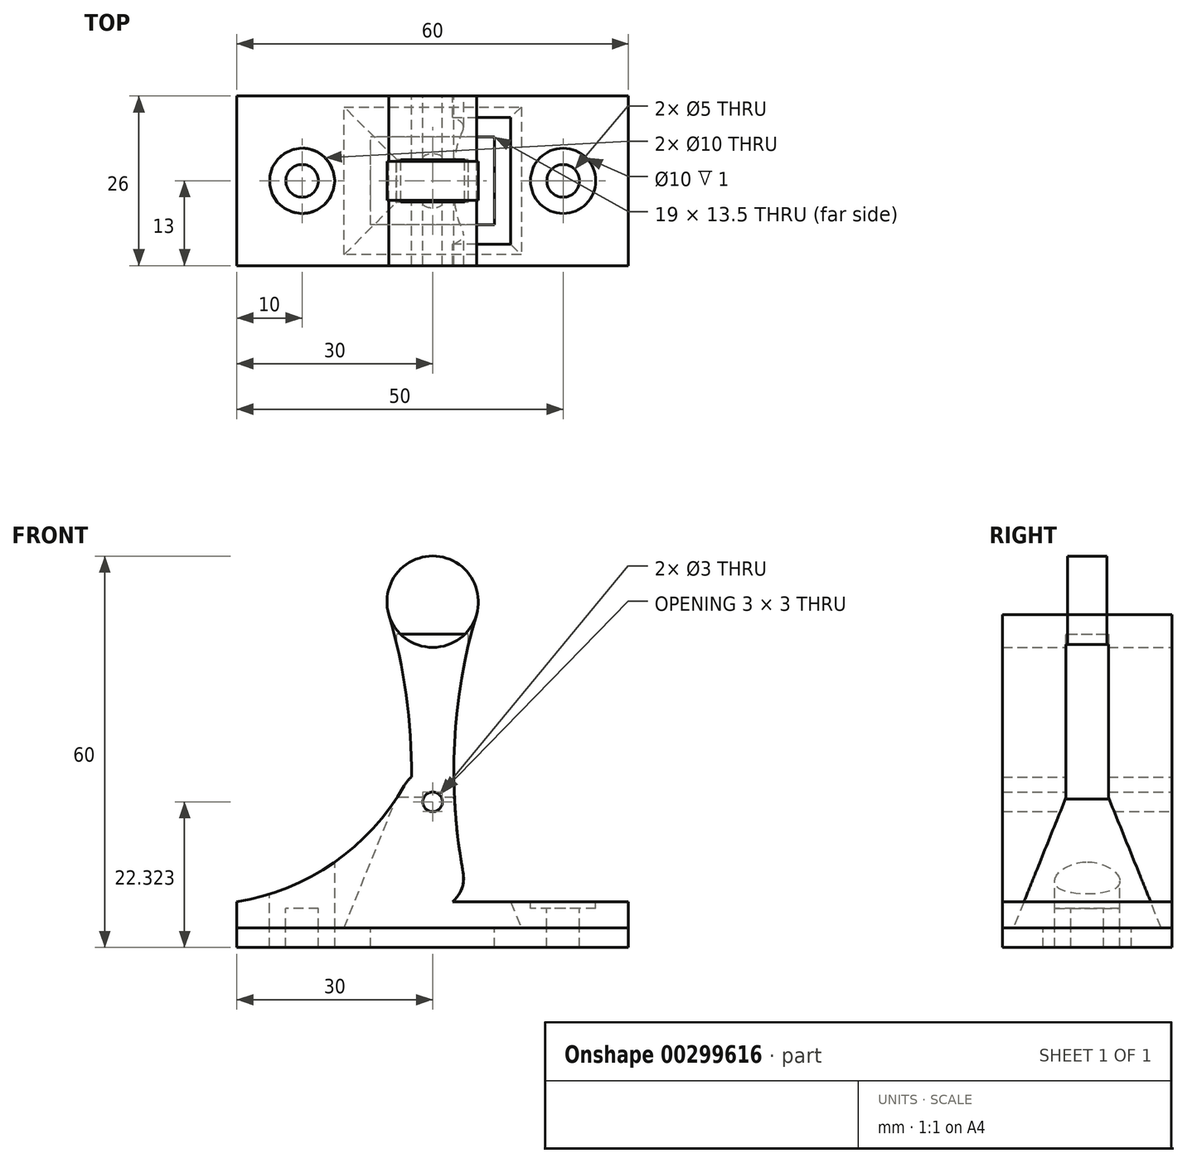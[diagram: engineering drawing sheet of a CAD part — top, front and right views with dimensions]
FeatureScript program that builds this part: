
annotation { "Feature Type Name" : "Feature", "Feature Type Description" : "" }
export const myFeature = defineFeature(function(context is Context, id is Id, definition is map)
    precondition{}
    {
        {
            var Q0;
            Q0=qCreatedBy(makeId("Front.planeOp"),FACE);
            var sketch = newSketch(context, id + "F0", { "sketchPlane" : qUnion([Q0])});
            skCircle(sketch, "E0", {"center": v(0, -12.35) * mm, "radius": 4.75 * mm});
            skCircle(sketch, "E1", {"center": v(0, 30) * mm, "radius": 7 * mm});
            skArc(sketch, "E2", {"start": v(-4.67, -11.48) * mm, "mid": v(-3.36, 8.39) * mm, "end": v(-6.71, 28.02) * mm});
            skArc(sketch, "E3.MirrorCS", {"start": v(4.67, -11.48) * mm, "mid": v(3.36, 8.39) * mm, "end": v(6.71, 28.02) * mm});
            skCircle(sketch, "E4", {"center": v(0, -0.68) * mm, "radius": 1.5 * mm});
            skCircle(sketch, "E5", {"center": v(0, -0.68) * mm, "radius": 5 * mm});
            skLineSegment(sketch, "E6.bottom", {"start": v(30, -20) * mm, "end": v(-30, -20) * mm});
            skLineSegment(sketch, "E6.top", {"start": v(30, -16) * mm, "end": v(-30, -16) * mm});
            skLineSegment(sketch, "E6.left", {"start": v(30, -20) * mm, "end": v(30, -16) * mm});
            skLineSegment(sketch, "E6.right", {"start": v(-30, -20) * mm, "end": v(-30, -16) * mm});
            skPoint(sketch, "E6.middle", {"position": v(0, -18) * mm});
            skArc(sketch, "E7", {"start": v(-30, -16) * mm, "mid": v(-15.16, -10) * mm, "end": v(-4.34, 1.8) * mm});
            skArc(sketch, "E8.MirrorCS", {"start": v(30, -16) * mm, "mid": v(15.16, -10) * mm, "end": v(4.34, 1.8) * mm});
            skSolve(sketch);
        }
        {
            var Q0;
            {var subQ0=sQuery(id+"F0.wireOp",EDGE,"E1");var subQ1=makeQuery(id+"F0.imprint","INTERSECT",VERTEX,{"derivedFrom":[subQ0,sQuery(id+"F0.wireOp",EDGE,"E2")]});Q0=makeQuery(id+"F0.imprint","IMPRINT",FACE,{"disambiguationData":[TD([[makeQuery(id+"F0.imprint","IMPRINT",EDGE,{"disambiguationData":[TD([[subQ1,-1.0]])],"derivedFrom":subQ0}),1.0]])]});}
            var Q1;
            {var subQ0=sQuery(id+"F0.wireOp",EDGE,"E3.MirrorCS");var subQ1=sQuery(id+"F0.wireOp",EDGE,"E0");var subQ2=makeQuery(id+"F0.imprint","INTERSECT",VERTEX,{"disambiguationData":[OD(1.0)],"derivedFrom":[subQ1,subQ0]});Q1=makeQuery(id+"F0.imprint","IMPRINT",FACE,{"disambiguationData":[TD([[makeQuery(id+"F0.imprint","IMPRINT",EDGE,{"disambiguationData":[TD([[subQ2,-1.0]])],"derivedFrom":subQ1}),-1.0]])]});}
            var Q2;
            {var subQ0=sQuery(id+"F0.wireOp",EDGE,"E3.MirrorCS");var subQ1=sQuery(id+"F0.wireOp",EDGE,"E0");var subQ2=makeQuery(id+"F0.imprint","INTERSECT",VERTEX,{"disambiguationData":[OD(1.0)],"derivedFrom":[subQ1,subQ0]});Q2=makeQuery(id+"F0.imprint","IMPRINT",FACE,{"disambiguationData":[TD([[makeQuery(id+"F0.imprint","IMPRINT",EDGE,{"disambiguationData":[TD([[subQ2,-1.0]])],"derivedFrom":subQ1}),1.0]])]});}
            var Q3;
            {var subQ0=sQuery(id+"F0.wireOp",EDGE,"E2");var subQ1=sQuery(id+"F0.wireOp",EDGE,"E1");var subQ2=makeQuery(id+"F0.imprint","INTERSECT",VERTEX,{"derivedFrom":[subQ1,subQ0]});Q3=makeQuery(id+"F0.imprint","IMPRINT",FACE,{"disambiguationData":[TD([[makeQuery(id+"F0.imprint","IMPRINT",EDGE,{"disambiguationData":[TD([[subQ2,-1.0]])],"derivedFrom":subQ1}),-1.0]])]});}
            var Q4;
            Q4=makeQuery(id+"F0.imprint","IMPRINT",FACE,{"disambiguationData":[TD([[makeQuery(id+"F0.imprint","IMPRINT",EDGE,{"derivedFrom":sQuery(id+"F0.wireOp",EDGE,"E4")}),-1.0]])]});
            var Q5;
            {var subQ0=sQuery(id+"F0.wireOp",EDGE,"E5");var subQ1=sQuery(id+"F0.wireOp",EDGE,"E0");var subQ2=makeQuery(id+"F0.imprint","INTERSECT",VERTEX,{"disambiguationData":[OD(0.0)],"derivedFrom":[subQ1,subQ0]});Q5=makeQuery(id+"F0.imprint","IMPRINT",FACE,{"disambiguationData":[TD([[makeQuery(id+"F0.imprint","IMPRINT",EDGE,{"disambiguationData":[TD([[subQ2,-1.0]])],"derivedFrom":subQ1}),1.0]])]});}
            var Q6;
            {var subQ0=sQuery(id+"F0.wireOp",EDGE,"E5");var subQ1=sQuery(id+"F0.wireOp",EDGE,"E0");var subQ2=makeQuery(id+"F0.imprint","INTERSECT",VERTEX,{"disambiguationData":[OD(1.0)],"derivedFrom":[subQ1,subQ0]});Q6=makeQuery(id+"F0.imprint","IMPRINT",FACE,{"disambiguationData":[TD([[makeQuery(id+"F0.imprint","IMPRINT",EDGE,{"disambiguationData":[TD([[subQ2,-1.0]])],"derivedFrom":subQ1}),-1.0]])]});}
            var Q7;
            {var subQ0=sQuery(id+"F0.wireOp",EDGE,"E6.top");var subQ1=sQuery(id+"F0.wireOp",EDGE,"E0");var subQ2=makeQuery(id+"F0.imprint","INTERSECT",VERTEX,{"disambiguationData":[OD(0.0)],"derivedFrom":[subQ1,subQ0]});Q7=makeQuery(id+"F0.imprint","IMPRINT",FACE,{"disambiguationData":[TD([[makeQuery(id+"F0.imprint","IMPRINT",EDGE,{"disambiguationData":[TD([[subQ2,-1.0]])],"derivedFrom":subQ1}),1.0]])]});}
            extrude(context, id + "F1", {"entities" : qUnion([Q0, Q1, Q2, Q3, Q4, Q5, Q6, Q7]), "depth" : 3 * mm, "hasSecondDirection" : true, "secondDirectionOppositeDirection" : true, "secondDirectionDepth" : 3 * mm});
        }
        {
            var Q0;
            Q0=makeQuery(id+"F0.imprint","IMPRINT",FACE,{"disambiguationData":[TD([[makeQuery(id+"F0.imprint","IMPRINT",EDGE,{"derivedFrom":sQuery(id+"F0.wireOp",EDGE,"E6.top")}),-1.0]])]});
            var Q1;
            {var subQ1=sQuery(id+"F0.wireOp",EDGE,"E0");var subQ3=sQuery(id+"F0.wireOp",EDGE,"E3.MirrorCS");var subQ8=makeQuery(id+"F0.imprint","INTERSECT",VERTEX,{"disambiguationData":[OD(1.0)],"derivedFrom":[subQ1,subQ3]});Q1=makeQuery(id+"F0.imprint","IMPRINT",FACE,{"disambiguationData":[TD([[makeQuery(id+"F0.imprint","IMPRINT",EDGE,{"disambiguationData":[TD([[subQ8,-1.0]])],"derivedFrom":subQ1}),1.0]])]});}
            var Q2;
            {var subQ0=sQuery(id+"F0.wireOp",EDGE,"E5");var subQ1=sQuery(id+"F0.wireOp",EDGE,"E0");var subQ2=makeQuery(id+"F0.imprint","INTERSECT",VERTEX,{"disambiguationData":[OD(1.0)],"derivedFrom":[subQ1,subQ0]});Q2=makeQuery(id+"F0.imprint","IMPRINT",FACE,{"disambiguationData":[TD([[makeQuery(id+"F0.imprint","IMPRINT",EDGE,{"disambiguationData":[TD([[subQ2,-1.0]])],"derivedFrom":subQ1}),-1.0]])]});}
            var Q3;
            {var subQ0=sQuery(id+"F0.wireOp",EDGE,"E3.MirrorCS");var subQ1=sQuery(id+"F0.wireOp",EDGE,"E0");var subQ2=makeQuery(id+"F0.imprint","INTERSECT",VERTEX,{"disambiguationData":[OD(1.0)],"derivedFrom":[subQ1,subQ0]});Q3=makeQuery(id+"F0.imprint","IMPRINT",FACE,{"disambiguationData":[TD([[makeQuery(id+"F0.imprint","IMPRINT",EDGE,{"disambiguationData":[TD([[subQ2,-1.0]])],"derivedFrom":subQ1}),-1.0]])]});}
            var Q4;
            {var subQ0=sQuery(id+"F0.wireOp",EDGE,"E5");var subQ1=sQuery(id+"F0.wireOp",EDGE,"E0");var subQ2=makeQuery(id+"F0.imprint","INTERSECT",VERTEX,{"disambiguationData":[OD(0.0)],"derivedFrom":[subQ1,subQ0]});Q4=makeQuery(id+"F0.imprint","IMPRINT",FACE,{"disambiguationData":[TD([[makeQuery(id+"F0.imprint","IMPRINT",EDGE,{"disambiguationData":[TD([[subQ2,-1.0]])],"derivedFrom":subQ1}),1.0]])]});}
            var Q5;
            Q5=makeQuery(id+"F0.imprint","IMPRINT",FACE,{"disambiguationData":[TD([[makeQuery(id+"F0.imprint","IMPRINT",EDGE,{"derivedFrom":sQuery(id+"F0.wireOp",EDGE,"E4")}),-1.0]])]});
            var Q6;
            {var subQ0=sQuery(id+"F0.wireOp",EDGE,"E5");var subQ1=sQuery(id+"F0.wireOp",EDGE,"E2");var subQ2=makeQuery(id+"F0.imprint","INTERSECT",VERTEX,{"disambiguationData":[OD(0.0)],"derivedFrom":[subQ1,subQ0]});Q6=makeQuery(id+"F0.imprint","IMPRINT",FACE,{"disambiguationData":[TD([[makeQuery(id+"F0.imprint","IMPRINT",EDGE,{"disambiguationData":[TD([[subQ2,1.0]])],"derivedFrom":subQ1}),1.0]])]});}
            var Q7;
            {var subQ0=sQuery(id+"F0.wireOp",EDGE,"E5");var subQ1=sQuery(id+"F0.wireOp",EDGE,"E3.MirrorCS");var subQ2=makeQuery(id+"F0.imprint","INTERSECT",VERTEX,{"disambiguationData":[OD(0.0)],"derivedFrom":[subQ1,subQ0]});Q7=makeQuery(id+"F0.imprint","IMPRINT",FACE,{"disambiguationData":[TD([[makeQuery(id+"F0.imprint","IMPRINT",EDGE,{"disambiguationData":[TD([[subQ2,1.0]])],"derivedFrom":subQ1}),-1.0]])]});}
            var Q8;
            Q8=makeQuery(id+"F0.imprint","IMPRINT",FACE,{"disambiguationData":[TD([[makeQuery(id+"F0.imprint","IMPRINT",EDGE,{"derivedFrom":sQuery(id+"F0.wireOp",EDGE,"E6.bottom")}),-1.0]])]});
            var Q9;
            {var subQ0=sQuery(id+"F0.wireOp",EDGE,"E6.top");var subQ1=sQuery(id+"F0.wireOp",EDGE,"E0");var subQ2=makeQuery(id+"F0.imprint","INTERSECT",VERTEX,{"disambiguationData":[OD(0.0)],"derivedFrom":[subQ1,subQ0]});Q9=makeQuery(id+"F0.imprint","IMPRINT",FACE,{"disambiguationData":[TD([[makeQuery(id+"F0.imprint","IMPRINT",EDGE,{"disambiguationData":[TD([[subQ2,-1.0]])],"derivedFrom":subQ1}),1.0]])]});}
            var Q10;
            {var subQ0=sQuery(id+"F0.wireOp",EDGE,"E8.MirrorCS");Q10=makeQuery(id+"F0.imprint","IMPRINT",FACE,{"disambiguationData":[TD([[makeQuery(id+"F0.imprint","IMPRINT",EDGE,{"derivedFrom":subQ0}),1.0]])]});}
            var Q11;
            {var subQ0=sQuery(id+"F0.wireOp",EDGE,"E7");Q11=makeQuery(id+"F0.imprint","IMPRINT",FACE,{"disambiguationData":[TD([[makeQuery(id+"F0.imprint","IMPRINT",EDGE,{"derivedFrom":subQ0}),-1.0]])]});}
            extrude(context, id + "F2", {"entities" : qUnion([Q0, Q1, Q2, Q3, Q4, Q5, Q6, Q7, Q8, Q9, Q10, Q11]), "depth" : 13 * mm, "hasSecondDirection" : true, "secondDirectionOppositeDirection" : true, "secondDirectionDepth" : 13 * mm});
        }
        {
            var Q0;
            Q0=qCreatedBy(makeId("Top.planeOp"),FACE);
            var sketch = newSketch(context, id + "F3", { "sketchPlane" : qUnion([Q0])});
            skLineSegment(sketch, "E9.bottom", {"start": v(5.5, -3.25) * mm, "end": v(-5.5, -3.25) * mm});
            skLineSegment(sketch, "E9.top", {"start": v(5.5, 3.25) * mm, "end": v(-5.5, 3.25) * mm});
            skLineSegment(sketch, "E9.left", {"start": v(5.5, -3.25) * mm, "end": v(5.5, 3.25) * mm});
            skLineSegment(sketch, "E9.right", {"start": v(-5.5, -3.25) * mm, "end": v(-5.5, 3.25) * mm});
            skPoint(sketch, "E9.middle", {"position": v(0, 0) * mm});
            skLineSegment(sketch, "E10.bottom", {"start": v(30, -13) * mm, "end": v(-30, -13) * mm});
            skLineSegment(sketch, "E10.top", {"start": v(30, 13) * mm, "end": v(-30, 13) * mm});
            skLineSegment(sketch, "E10.left", {"start": v(30, -13) * mm, "end": v(30, 13) * mm});
            skLineSegment(sketch, "E10.right", {"start": v(-30, -13) * mm, "end": v(-30, 13) * mm});
            skLineSegment(sketch, "E11.bottom", {"start": v(9.5, -6.75) * mm, "end": v(-9.5, -6.75) * mm});
            skLineSegment(sketch, "E11.top", {"start": v(9.5, 6.75) * mm, "end": v(-9.5, 6.75) * mm});
            skLineSegment(sketch, "E11.left", {"start": v(9.5, -6.75) * mm, "end": v(9.5, 6.75) * mm});
            skLineSegment(sketch, "E11.right", {"start": v(-9.5, -6.75) * mm, "end": v(-9.5, 6.75) * mm});
            skCircle(sketch, "E12", {"center": v(20, 0) * mm, "radius": 2.5 * mm});
            skCircle(sketch, "E13", {"center": v(20, 0) * mm, "radius": 5 * mm});
            skCircle(sketch, "E14.MirrorC", {"center": v(-20, 0) * mm, "radius": 2.5 * mm});
            skCircle(sketch, "E15.MirrorC", {"center": v(-20, 0) * mm, "radius": 5 * mm});
            skSolve(sketch);
        }
        {
            var Q0;
            Q0=makeQuery(id+"F3.imprint","IMPRINT",FACE,{"disambiguationData":[TD([[makeQuery(id+"F3.imprint","IMPRINT",EDGE,{"derivedFrom":sQuery(id+"F3.wireOp",EDGE,"E9.bottom")}),-1.0]])]});
            extrude(context, id + "F4", {"entities" : qUnion([Q0]), "operationType" : NewBodyOperationType.REMOVE, "oppositeDirection" : true, "depth" : 25 * mm, "hasDraft" : true, "draftAngle" : 22 * degree, "hasSecondDirection" : true, "secondDirectionOppositeDirection" : false, "secondDirectionDepth" : 25 * mm});
        }
        {
            var Q0;
            Q0=makeQuery(id+"F3.imprint","IMPRINT",FACE,{"disambiguationData":[TD([[makeQuery(id+"F3.imprint","IMPRINT",EDGE,{"derivedFrom":sQuery(id+"F3.wireOp",EDGE,"E10.bottom")}),-1.0]])]});
            var Q1;
            Q1=makeQuery(id+"F3.imprint","IMPRINT",FACE,{"disambiguationData":[TD([[makeQuery(id+"F3.imprint","IMPRINT",EDGE,{"derivedFrom":sQuery(id+"F3.wireOp",EDGE,"E12")}),-1.0]])]});
            var Q2;
            Q2=makeQuery(id+"F3.imprint","IMPRINT",FACE,{"disambiguationData":[TD([[makeQuery(id+"F3.imprint","IMPRINT",EDGE,{"derivedFrom":sQuery(id+"F3.wireOp",EDGE,"E14.MirrorC")}),1.0]])]});
            extrude(context, id + "F5", {"entities" : qUnion([Q0, Q1, Q2]), "oppositeDirection" : true, "depth" : 23 * mm, "hasSecondDirection" : true, "secondDirectionOppositeDirection" : true, "secondDirectionDepth" : 20 * mm});
        }
        {
            var Q0;
            Q0=makeQuery(id+"F3.imprint","IMPRINT",FACE,{"disambiguationData":[TD([[makeQuery(id+"F3.imprint","IMPRINT",EDGE,{"derivedFrom":sQuery(id+"F3.wireOp",EDGE,"E14.MirrorC")}),-1.0]])]});
            var Q1;
            Q1=makeQuery(id+"F3.imprint","IMPRINT",FACE,{"disambiguationData":[TD([[makeQuery(id+"F3.imprint","IMPRINT",EDGE,{"derivedFrom":sQuery(id+"F3.wireOp",EDGE,"E12")}),1.0]])]});
            extrude(context, id + "F6", {"entities" : qUnion([Q0, Q1]), "operationType" : NewBodyOperationType.REMOVE, "oppositeDirection" : true, "depth" : 25 * mm});
        }
        {
            var Q0;
            Q0=makeQuery(id+"F3.imprint","IMPRINT",FACE,{"disambiguationData":[TD([[makeQuery(id+"F3.imprint","IMPRINT",EDGE,{"derivedFrom":sQuery(id+"F3.wireOp",EDGE,"E14.MirrorC")}),1.0]])]});
            var Q1;
            Q1=makeQuery(id+"F3.imprint","IMPRINT",FACE,{"disambiguationData":[TD([[makeQuery(id+"F3.imprint","IMPRINT",EDGE,{"derivedFrom":sQuery(id+"F3.wireOp",EDGE,"E12")}),-1.0]])]});
            extrude(context, id + "F7", {"entities" : qUnion([Q0, Q1]), "operationType" : NewBodyOperationType.REMOVE, "oppositeDirection" : true, "depth" : 17 * mm});
        }
    });
